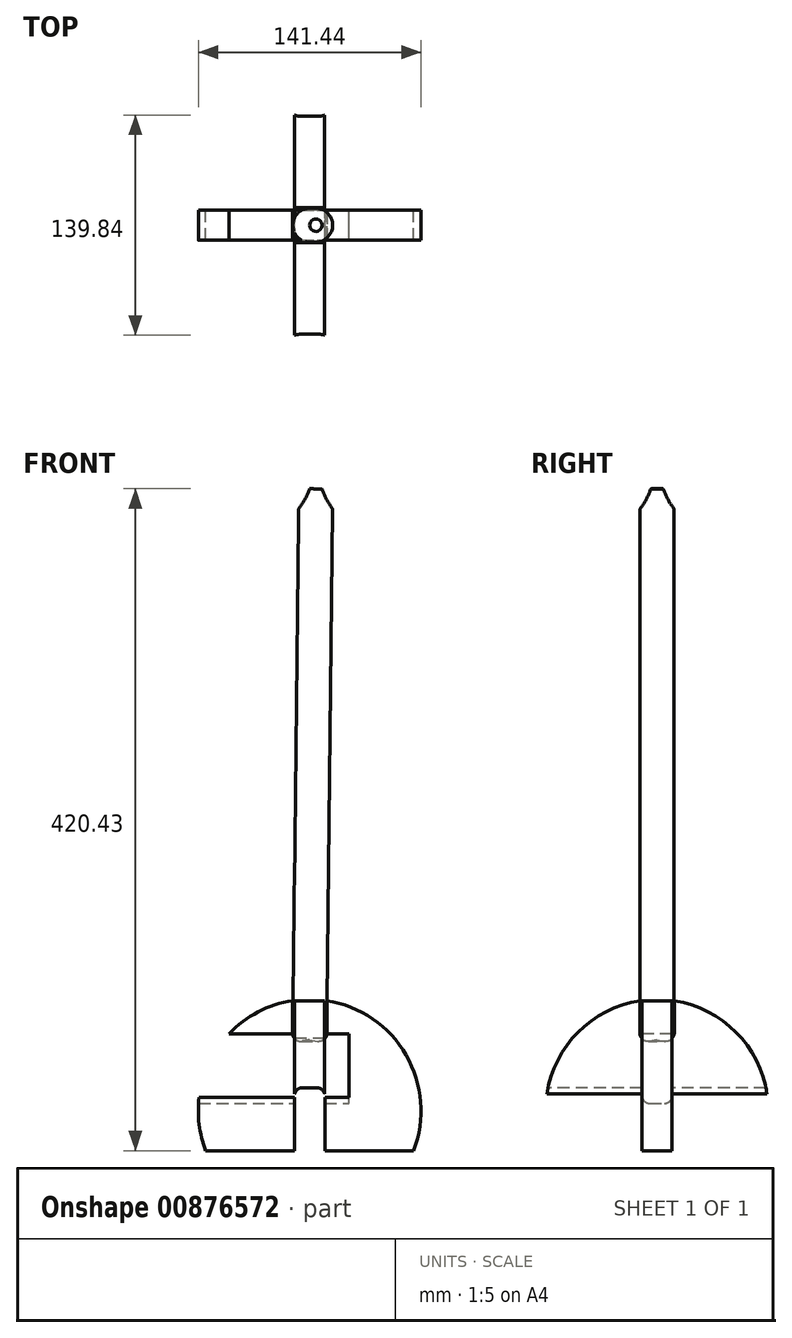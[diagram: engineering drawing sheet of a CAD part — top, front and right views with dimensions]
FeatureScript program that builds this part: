
annotation { "Feature Type Name" : "Feature", "Feature Type Description" : "" }
export const myFeature = defineFeature(function(context is Context, id is Id, definition is map)
    precondition{}
    {
        {
            var Q0;
            Q0=qCreatedBy(makeId("Front.planeOp"),FACE);
            var sketch = newSketch(context, id + "F0", { "sketchPlane" : qUnion([Q0])});
            skLineSegment(sketch, "E0", {"start": v(-66, 0) * mm, "end": v(44, 0) * mm});
            skLineSegment(sketch, "E1", {"start": v(44, 0) * mm, "end": v(-11, 95.26) * mm});
            skLineSegment(sketch, "E2", {"start": v(-11, 95.26) * mm, "end": v(-66, 0) * mm});
            skLineSegment(sketch, "E3.MirrorCS", {"start": v(-44, 0) * mm, "end": v(11, 95.26) * mm});
            skLineSegment(sketch, "E4.MirrorCS", {"start": v(11, 95.26) * mm, "end": v(66, 0) * mm});
            skLineSegment(sketch, "E5.MirrorCS", {"start": v(66, 0) * mm, "end": v(-44, 0) * mm});
            skArc(sketch, "E6", {"start": v(66, 0) * mm, "mid": v(0, 96.12) * mm, "end": v(-66, 0) * mm});
            skSolve(sketch);
        }
        {
            var Q0;
            Q0=qSketchRegion(id+"F0",true);
            extrude(context, id + "F1", {"entities" : qUnion([Q0]), "depth" : (19 / 2) * mm, "offsetDistance" : 25 * mm, "hasSecondDirection" : true, "secondDirectionOppositeDirection" : true, "secondDirectionDepth" : (19 / 2) * mm});
        }
        {
            var Q0;
            Q0=qCreatedBy(makeId("Front.planeOp"),FACE);
            var sketch = newSketch(context, id + "F2", { "sketchPlane" : qUnion([Q0])});
            skLineSegment(sketch, "E7.bottom", {"start": v(11, 70) * mm, "end": v(-11, 70) * mm});
            skLineSegment(sketch, "E7.top", {"start": v(11, 124.26) * mm, "end": v(-11, 124.26) * mm});
            skLineSegment(sketch, "E7.left", {"start": v(11, 70) * mm, "end": v(11, 124.26) * mm});
            skLineSegment(sketch, "E7.right", {"start": v(-11, 70) * mm, "end": v(-11, 124.26) * mm});
            skPoint(sketch, "E7.middle", {"position": v(0, 97.13) * mm});
            skSolve(sketch);
        }
        {
            var Q0;
            Q0=qSketchRegion(id+"F2",true);
            extrude(context, id + "F3", {"entities" : qUnion([Q0]), "operationType" : NewBodyOperationType.REMOVE, "endBound" : BoundingType.THROUGH_ALL, "oppositeDirection" : true, "depth" : 25 * mm, "offsetDistance" : 25 * mm, "hasSecondDirection" : true, "secondDirectionBound" : SecondDirectionBoundingType.THROUGH_ALL, "secondDirectionOppositeDirection" : false, "secondDirectionDepth" : 25 * mm});
        }
        {
            var Q0;
            Q0=makeQuery(id+"F3.boolean.opBoolean","COPY",EDGE,{"derivedFrom":makeQuery(id+"F3.opExtrude","SWEPT_EDGE",EDGE,{"disambiguationData":[OSD([sQuery(id+"F2.wireOp",EDGE,"E7.bottom"),sQuery(id+"F2.wireOp",EDGE,"E7.right")])]})});
            var Q1;
            Q1=makeQuery(id+"F3.boolean.opBoolean","COPY",EDGE,{"derivedFrom":makeQuery(id+"F3.opExtrude","SWEPT_EDGE",EDGE,{"disambiguationData":[OSD([sQuery(id+"F2.wireOp",EDGE,"E7.bottom"),sQuery(id+"F2.wireOp",EDGE,"E7.left")])]})});
            fillet(context, id + "F4", {"entities" : qUnion([Q0, Q1]), "radius" : 5 * mm, "tangentPropagation" : true, "allowEdgeOverflow" : false});
        }
        {
            var Q0;
            Q0=qCreatedBy(makeId("Right.planeOp"),FACE);
            var Q1;
            Q1=qCreatedBy(makeId("Front.planeOp"),FACE);
            cPlane(context, id + "F5", {"entities" : qUnion([Q0, Q1]), "cplaneType" : CPlaneType.MID_PLANE, "offset" : 25 * mm, "width" : 150 * mm, "height" : 150 * mm});
        }
        {
            var Q0;
            Q0=makeQuery(id+"F1.opExtrude","SWEPT_BODY",BODY,{"disambiguationData":[OSD([sQuery(id+"F0.wireOp",EDGE,"E0"),sQuery(id+"F0.wireOp",EDGE,"E1"),sQuery(id+"F0.wireOp",EDGE,"E2"),sQuery(id+"F0.wireOp",EDGE,"E3.MirrorCS"),sQuery(id+"F0.wireOp",EDGE,"E4.MirrorCS"),sQuery(id+"F0.wireOp",EDGE,"E5.MirrorCS")])]});
            var Q1;
            Q1=qCreatedBy(id+"F5.planeOp",FACE);
            mirror(context, id + "F6", {"entities" : qUnion([Q0]), "mirrorPlane" : qUnion([Q1])});
        }
        {
            var Q0;
            Q0=qCreatedBy(makeId("Front.planeOp"),FACE);
            var sketch = newSketch(context, id + "F7", { "sketchPlane" : qUnion([Q0])});
            skLineSegment(sketch, "E8", {"start": v(0, 0) * mm, "end": v(0, 70) * mm, "construction": true});
            skLineSegment(sketch, "E9", {"start": v(0, 0) * mm, "end": v(0, 35) * mm, "construction": true});
            skLineSegment(sketch, "E10.bottom", {"start": v(9.6, 0) * mm, "end": v(-9.6, 0) * mm});
            skLineSegment(sketch, "E10.top", {"start": v(9.6, 35) * mm, "end": v(-9.6, 35) * mm, "construction": true});
            skLineSegment(sketch, "E10.left", {"start": v(9.6, 0) * mm, "end": v(9.6, 35) * mm});
            skLineSegment(sketch, "E10.right", {"start": v(-9.6, 0) * mm, "end": v(-9.6, 35) * mm});
            skPoint(sketch, "E10.middle", {"position": v(0, 17.5) * mm});
            skLineSegment(sketch, "E11.top", {"start": v(-4.6, 40) * mm, "end": v(4.6, 40) * mm});
            skLineSegment(sketch, "E11.left", {"start": v(-9.6, 35) * mm, "end": v(-9.6, 35) * mm});
            skLineSegment(sketch, "E11.right", {"start": v(9.6, 35) * mm, "end": v(9.6, 35) * mm});
            skPoint(sketch, "E12.visualSharp", {"position": v(-9.6, 40) * mm});
            skArc(sketch, "E12.filletArc", {"start": v(-4.6, 40) * mm, "mid": v(-8.14, 38.54) * mm, "end": v(-9.6, 35) * mm});
            skPoint(sketch, "E13.visualSharp", {"position": v(9.6, 40) * mm});
            skArc(sketch, "E13.filletArc", {"start": v(9.6, 35) * mm, "mid": v(8.14, 38.54) * mm, "end": v(4.6, 40) * mm});
            skSolve(sketch);
        }
        {
            var Q0;
            Q0=qSketchRegion(id+"F7",true);
            extrude(context, id + "F8", {"entities" : qUnion([Q0]), "operationType" : NewBodyOperationType.REMOVE, "endBound" : BoundingType.THROUGH_ALL, "oppositeDirection" : true, "depth" : 25 * mm, "offsetDistance" : 25 * mm, "hasSecondDirection" : true, "secondDirectionBound" : SecondDirectionBoundingType.THROUGH_ALL, "secondDirectionOppositeDirection" : false, "secondDirectionDepth" : 25 * mm});
        }
        {
            var Q0;
            Q0=qCreatedBy(makeId("Right.planeOp"),FACE);
            var sketch = newSketch(context, id + "F9", { "sketchPlane" : qUnion([Q0])});
            skLineSegment(sketch, "E14", {"start": v(0, 0) * mm, "end": v(0, 70) * mm, "construction": true});
            skLineSegment(sketch, "E15", {"start": v(0, 70) * mm, "end": v(0, 35) * mm, "construction": true});
            skLineSegment(sketch, "E16.bottom", {"start": v(9.6, 35) * mm, "end": v(-9.6, 35) * mm, "construction": true});
            skLineSegment(sketch, "E16.top", {"start": v(9.6, 70) * mm, "end": v(-9.6, 70) * mm});
            skLineSegment(sketch, "E16.left", {"start": v(9.6, 35) * mm, "end": v(9.6, 70) * mm});
            skLineSegment(sketch, "E16.right", {"start": v(-9.6, 35) * mm, "end": v(-9.6, 70) * mm});
            skPoint(sketch, "E16.middle", {"position": v(0, 52.5) * mm});
            skLineSegment(sketch, "E17.bottom", {"start": v(-9.6, 35) * mm, "end": v(9.6, 35) * mm});
            skLineSegment(sketch, "E17.top", {"start": v(-4.6, 30) * mm, "end": v(4.6, 30) * mm});
            skLineSegment(sketch, "E17.left", {"start": v(-9.6, 35) * mm, "end": v(-9.6, 35) * mm});
            skLineSegment(sketch, "E17.right", {"start": v(9.6, 35) * mm, "end": v(9.6, 35) * mm});
            skLineSegment(sketch, "E18.bottom", {"start": v(-9.6, 70) * mm, "end": v(9.6, 70) * mm});
            skLineSegment(sketch, "E18.top", {"start": v(-9.6, 74.3) * mm, "end": v(9.6, 74.3) * mm});
            skLineSegment(sketch, "E18.left", {"start": v(-9.6, 70) * mm, "end": v(-9.6, 74.3) * mm});
            skLineSegment(sketch, "E18.right", {"start": v(9.6, 70) * mm, "end": v(9.6, 74.3) * mm});
            skPoint(sketch, "E19.visualSharp", {"position": v(-9.6, 30) * mm});
            skArc(sketch, "E19.filletArc", {"start": v(-9.6, 35) * mm, "mid": v(-8.14, 31.46) * mm, "end": v(-4.6, 30) * mm});
            skPoint(sketch, "E20.visualSharp", {"position": v(9.6, 30) * mm});
            skArc(sketch, "E20.filletArc", {"start": v(4.6, 30) * mm, "mid": v(8.14, 31.46) * mm, "end": v(9.6, 35) * mm});
            skSolve(sketch);
        }
        {
            var Q0;
            Q0=qSketchRegion(id+"F9",true);
            extrude(context, id + "F10", {"entities" : qUnion([Q0]), "operationType" : NewBodyOperationType.REMOVE, "endBound" : BoundingType.THROUGH_ALL, "oppositeDirection" : true, "depth" : 25 * mm, "offsetDistance" : 25 * mm, "hasSecondDirection" : true, "secondDirectionOppositeDirection" : false, "secondDirectionDepth" : 25 * mm});
        }
        {
            var Q0;
            Q0=qCreatedBy(makeId("Front.planeOp"),FACE);
            var sketch = newSketch(context, id + "F11", { "sketchPlane" : qUnion([Q0])});
            skLineSegment(sketch, "E21.bottom", {"start": v(0, 70.41) * mm, "end": v(-4.87, 69.53) * mm});
            skLineSegment(sketch, "E21.left", {"start": v(0, 70.41) * mm, "end": v(3.95, 420.39) * mm});
            skLineSegment(sketch, "E21.right", {"start": v(-10.76, 74.5) * mm, "end": v(-7, 407.14) * mm});
            skPoint(sketch, "E22.visualSharp", {"position": v(-10.82, 68.45) * mm});
            skArc(sketch, "E22.filletArc", {"start": v(-10.76, 74.5) * mm, "mid": v(-8.98, 70.63) * mm, "end": v(-4.87, 69.53) * mm});
            skLineSegment(sketch, "E23", {"start": v(3.95, 420.39) * mm, "end": v(0, 420.43) * mm});
            skArc(sketch, "E24", {"start": v(-6.59, 408.34) * mm, "mid": v(-2.81, 414.13) * mm, "end": v(0, 420.43) * mm});
            skPoint(sketch, "E25.visualSharp", {"position": v(-7, 407.82) * mm});
            skArc(sketch, "E25.filletArc", {"start": v(-6.59, 408.34) * mm, "mid": v(-6.9, 407.78) * mm, "end": v(-7, 407.14) * mm});
            skSolve(sketch);
        }
        {
            var Q0;
            Q0=makeQuery(id+"F11.imprint","IMPRINT",FACE,{"disambiguationData":[TD([[makeQuery(id+"F11.imprint","IMPRINT",EDGE,{"derivedFrom":sQuery(id+"F11.wireOp",EDGE,"E21.bottom")}),-1.0]])]});
            var Q1;
            Q1=sQuery(id+"F11.wireOp",EDGE,"E21.left");
            revolve(context, id + "F12", {"surfaceOperationType" : NewSurfaceOperationType.NEW, "entities" : qUnion([Q0]), "axis" : qUnion([Q1]), "revolveType" : RevolveType.FULL});
        }
    });
